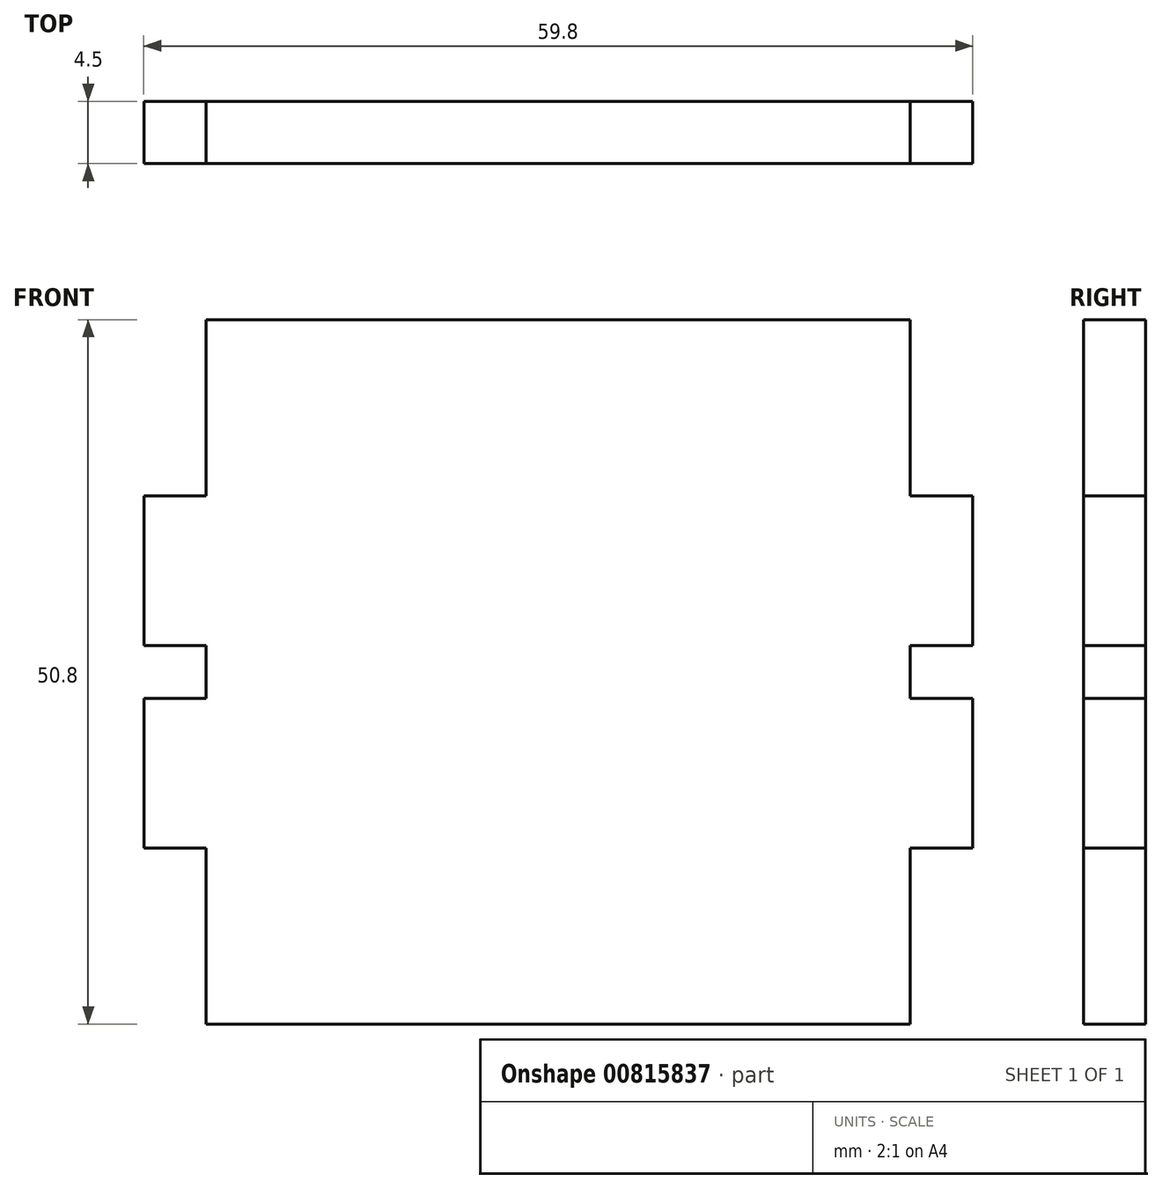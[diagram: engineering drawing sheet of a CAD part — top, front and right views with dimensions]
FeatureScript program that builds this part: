
annotation { "Feature Type Name" : "Feature", "Feature Type Description" : "" }
export const myFeature = defineFeature(function(context is Context, id is Id, definition is map)
    precondition{}
    {
        {
            var Q0;
            Q0=qCreatedBy(makeId("Front.planeOp"),FACE);
            var sketch = newSketch(context, id + "F0", { "sketchPlane" : qUnion([Q0])});
            skLineSegment(sketch, "E0.bottom", {"start": v(25.4, -25.4) * mm, "end": v(-25.4, -25.4) * mm});
            skLineSegment(sketch, "E0.top", {"start": v(25.4, 25.4) * mm, "end": v(-25.4, 25.4) * mm});
            skLineSegment(sketch, "E0.left", {"start": v(25.4, -25.4) * mm, "end": v(25.4, -12.7) * mm});
            skLineSegment(sketch, "E0.right", {"start": v(-25.4, -25.4) * mm, "end": v(-25.4, -12.7) * mm});
            skPoint(sketch, "E0.middle", {"position": v(0, 0) * mm});
            skLineSegment(sketch, "E1.bottom", {"start": v(29.9, -12.7) * mm, "end": v(25.4, -12.7) * mm});
            skLineSegment(sketch, "E1.top", {"start": v(29.9, 12.7) * mm, "end": v(25.4, 12.7) * mm});
            skLineSegment(sketch, "E1.left", {"start": v(29.9, -12.7) * mm, "end": v(29.9, -1.9) * mm});
            skPoint(sketch, "E1.middle", {"position": v(25.4, 0) * mm});
            skPoint(sketch, "E1.right.end.orphan", {"position": v(20.9, 12.7) * mm});
            skPoint(sketch, "E2.orphan", {"position": v(20.9, -12.7) * mm});
            skLineSegment(sketch, "E3.MirrorCS", {"start": v(-29.9, 12.7) * mm, "end": v(-25.4, 12.7) * mm});
            skLineSegment(sketch, "E4.MirrorCS", {"start": v(-29.9, -12.7) * mm, "end": v(-29.9, -1.9) * mm});
            skLineSegment(sketch, "E5.MirrorCS", {"start": v(-29.9, -12.7) * mm, "end": v(-25.4, -12.7) * mm});
            skLineSegment(sketch, "E6.trimOffspring", {"start": v(-25.4, 12.7) * mm, "end": v(-25.4, 25.4) * mm});
            skLineSegment(sketch, "E7.trimOffspring", {"start": v(25.4, 12.7) * mm, "end": v(25.4, 25.4) * mm});
            skLineSegment(sketch, "E8.bottom", {"start": v(25.4, -1.9) * mm, "end": v(29.9, -1.9) * mm});
            skLineSegment(sketch, "E8.top", {"start": v(25.4, 1.9) * mm, "end": v(29.9, 1.9) * mm});
            skLineSegment(sketch, "E8.left", {"start": v(25.4, -1.9) * mm, "end": v(25.4, 1.9) * mm});
            skPoint(sketch, "E8.middle", {"position": v(29.9, 0) * mm});
            skPoint(sketch, "E8.right.end.orphan", {"position": v(34.4, 1.9) * mm});
            skPoint(sketch, "E9.orphan", {"position": v(34.4, -1.9) * mm});
            skLineSegment(sketch, "E10.MirrorCS", {"start": v(-25.4, 1.9) * mm, "end": v(-29.9, 1.9) * mm});
            skLineSegment(sketch, "E11.MirrorCS", {"start": v(-25.4, -1.9) * mm, "end": v(-29.9, -1.9) * mm});
            skLineSegment(sketch, "E12.MirrorCS", {"start": v(-25.4, -1.9) * mm, "end": v(-25.4, 1.9) * mm});
            skLineSegment(sketch, "E13.trimOffspring", {"start": v(-29.9, 1.9) * mm, "end": v(-29.9, 12.7) * mm});
            skLineSegment(sketch, "E14.trimOffspring", {"start": v(29.9, 1.9) * mm, "end": v(29.9, 12.7) * mm});
            skSolve(sketch);
        }
        {
            var Q0;
            Q0 = qSketchRegion(id + "F0", true);
            extrude(context, id + "F1", {"entities" : qUnion([Q0]), "depth" : 4.5 * mm, "offsetDistance" : 25.4 * mm, "symmetric" : true});
        }
    });
